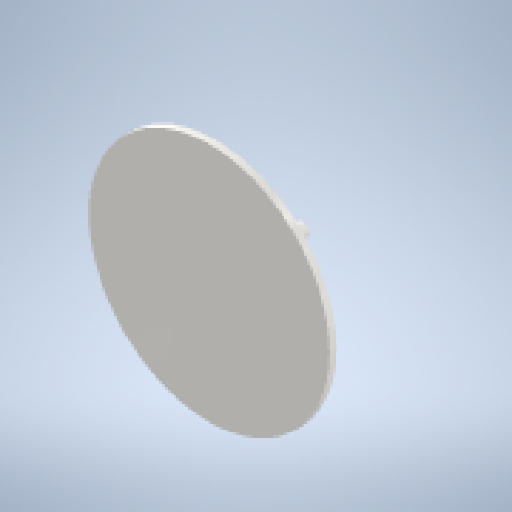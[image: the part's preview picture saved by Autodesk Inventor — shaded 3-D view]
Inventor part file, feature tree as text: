
AUTODESK INVENTOR PART (.ipt)
format: ipt  version: 2023 (Build 270158000, 158)  size: 673,280 bytes
history: native  units: mm (DEFAULTED — no unit token found)
features: sketch x4, extrude x3, plane x3, other x3, projected_geometry x2
ambient origin geometry x8: Origin, YZ Plane, XZ Plane, XY Plane, X Axis, Y Axis, Z Axis, Center Point
bodies: Solid1 (feature_tree)
feature tree (15):
  extrude  "Extrusion1"  Depth=10.0mm TaperAngle=0.0deg
  plane  "Work Plane2"
  plane  "Work Plane8"
  plane  "Work Plane9"
  other  "Spur Gear"
  extrude  "Extrusion2"  Depth=10.0mm TaperAngle=0.0deg
  extrude  "Extrusion3"  Depth=0.551157mm TaperAngle=0.0deg
  sketch  "Sketch1"  dims[d0=118.0mm d1=10.0mm d2=0.0mm]
  sketch  "Sketch2"  dims[d3=114.0mm d4=10.0mm d5=0.0mm]
  other  "Srf1"
  sketch  "Sketch3"  dims[d16=80.0mm d17=0.0mm d34=0.551157mm]
  projected_geometry  "Projected Loop1"
  sketch  "Sketch4"  dims[d39=0.0mm d41=0.0mm d43=80.0mm d46=80.0mm d47=0.0mm d48=0.0mm d49=9.8mm d50=35.0mm d51=0.0mm d52=180.0mm d53=5.0mm d54=0.0mm d55=0.5mm d56=0.872665mm]
  projected_geometry  "Projected Loop2"
  other  "Pitch Diameter"
